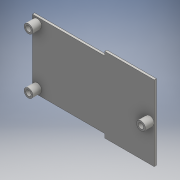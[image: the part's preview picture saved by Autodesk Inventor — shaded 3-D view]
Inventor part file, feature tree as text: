
AUTODESK INVENTOR PART (.ipt)
format: ipt  version: 2016 (Build 200138000, 138)  size: 145,408 bytes
history: native  units: mm
features: extrude x2, sketch x2, hole x1
ambient origin geometry x8: Origin, YZ Plane, XZ Plane, XY Plane, X Axis, Y Axis, Z Axis, Center Point
bodies: Solid1 (feature_tree)
feature tree (5):
  extrude  "Extrusion1"  Depth=56.0mm
  sketch  "Sketch3"  dims[d17=2.5mm d18=0.0mm d19=56.0mm]
  extrude  "Extrusion3"  Depth=4.5mm
  hole  "Hole1"  [1 undecoded]
  sketch  "Sketch4"  dims[d20=4.5mm d21=4.5mm d22=56.0mm d23=4.4mm d24=6.0mm d25=6.0mm d26=59.5mm d28=18.0mm d29=4.4mm d33=5.074mm d34=6.0mm d35=10.0mm d36=6.0mm d37=6.5mm d38=5.5mm d39=10.0mm d40=10.0mm d41=0.0mm d42=4.4mm d43=4.4mm d44=4.5mm d45=6.0mm d46=4.0mm d47=2.0mm d48=90.0deg d49=2.0mm d50=0.0mm d54=76.0mm d55=81.742mm d56=85.0mm d57=63.0mm d58=6.5mm d59=5.5mm]
note: 1 required parameter value undecoded (feature->parameter linkage not recoverable at this tier; creation-order binding heuristic only, values carry confidence <= 0.55)
